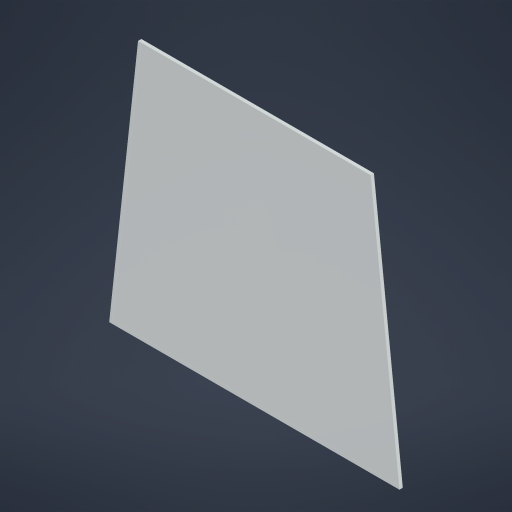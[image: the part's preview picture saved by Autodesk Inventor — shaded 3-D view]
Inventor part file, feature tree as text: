
AUTODESK INVENTOR PART (.ipt)
format: ipt  version: 2023.2 (Build 272271000, 271)  size: 264,192 bytes
history: native  units: mm
features: sketch x2
ambient origin geometry x8: Origin, YZ Plane, XZ Plane, XY Plane, X Axis, Y Axis, Z Axis, Center Point
bodies: Body1 (feature_tree)
feature tree (2):
  sketch  "Sketch1"  dims[d229=90.0mm]
  sketch  "Sketch2"  dims[d232=16.0mm d233=12.0mm d234=12.0mm d235=4.0mm d237=4.0mm d238=0.0mm d239=14.0mm d241=130.0mm d242=100.0mm d243=17.0mm d245=8.0mm d246=10.0mm d247=80.0mm d249=10.0mm d250=4.0mm d251=0.0mm d256=2.5mm d257=0.0mm d258=1.5mm d259=0.0mm d260=2.5mm d261=0.0mm d9=0.5mm d10=0.872665mm d11=0.5mm d12=0.872665mm d13=0.5mm d14=0.872665mm d27=0.5mm d28=0.872665mm d29=0.5mm d30=0.872665mm d88=0.5mm d89=0.872665mm d90=0.5mm d91=0.872665mm d116=0.5mm d117=0.872665mm d118=0.5mm d119=0.872665mm d154=0.5mm d155=0.872665mm d156=0.5mm d157=0.872665mm d181=0.5mm d182=0.872665mm d183=0.5mm d184=0.872665mm d221=0.5mm d222=0.872665mm d223=0.5mm d224=0.872665mm d262=0.5mm d263=0.872665mm]
